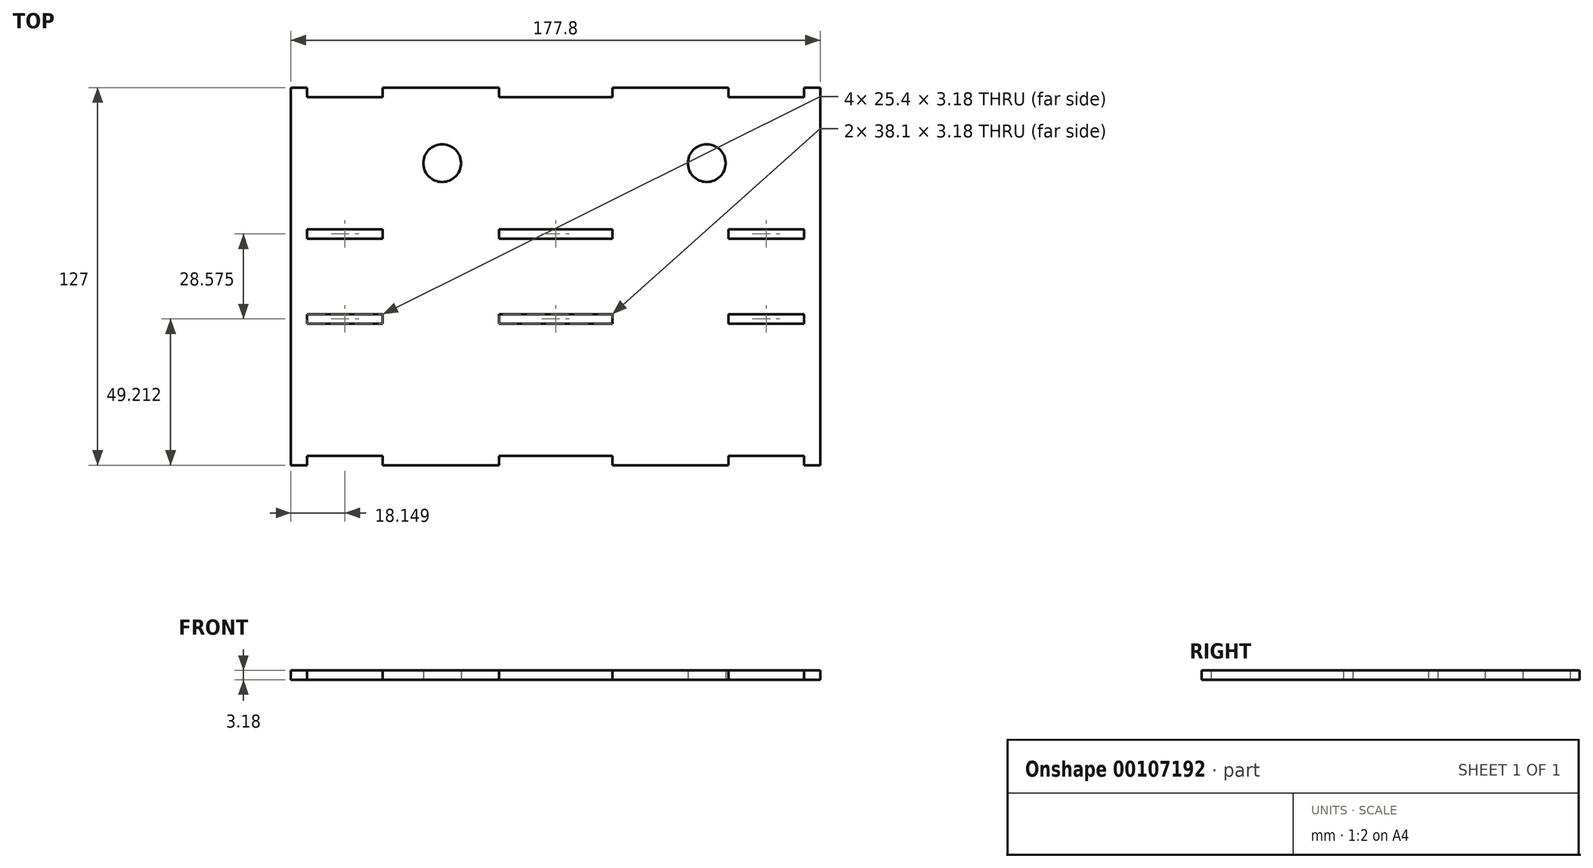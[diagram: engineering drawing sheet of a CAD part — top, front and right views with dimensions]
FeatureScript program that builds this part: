
annotation { "Feature Type Name" : "Feature", "Feature Type Description" : "" }
export const myFeature = defineFeature(function(context is Context, id is Id, definition is map)
    precondition{}
    {
        {
            var Q0;
            Q0=qCreatedBy(makeId("Top.planeOp"),FACE);
            var sketch = newSketch(context, id + "F0", { "sketchPlane" : qUnion([Q0])});
            skCircle(sketch, "E0", {"center": v(63.5, 38.1) * mm, "radius": 6.35 * mm});
            skCircle(sketch, "E1", {"center": v(-25.4, 38.1) * mm, "radius": 6.35 * mm});
            skLineSegment(sketch, "E2", {"start": v(-76.2, 63.5) * mm, "end": v(-76.2, -63.5) * mm});
            skLineSegment(sketch, "E3.bottom", {"start": v(-76.2, 63.5) * mm, "end": v(-70.75, 63.5) * mm});
            skLineSegment(sketch, "E3.left", {"start": v(-76.2, 63.5) * mm, "end": v(-76.2, -88.9) * mm});
            skLineSegment(sketch, "E3.right", {"start": v(101.6, 63.5) * mm, "end": v(101.6, -63.5) * mm});
            skCircle(sketch, "E4.MirrorC", {"center": v(63.5, -38.1) * mm, "radius": 6.35 * mm});
            skCircle(sketch, "E5.MirrorC", {"center": v(-25.4, -38.1) * mm, "radius": 6.35 * mm});
            skPoint(sketch, "E6", {"position": v(12.7, 76.2) * mm});
            skPoint(sketch, "E7", {"position": v(12.7, 63.5) * mm});
            skLineSegment(sketch, "E8.MirrorCS", {"start": v(70.75, 63.5) * mm, "end": v(70.75, 60.32) * mm});
            skLineSegment(sketch, "E9.MirrorCS", {"start": v(31.75, 60.32) * mm, "end": v(-6.35, 60.32) * mm});
            skLineSegment(sketch, "E10.MirrorCS", {"start": v(-70.75, 60.32) * mm, "end": v(-45.35, 60.32) * mm});
            skLineSegment(sketch, "E11.MirrorCS", {"start": v(-6.35, 63.5) * mm, "end": v(-6.35, 60.32) * mm});
            skLineSegment(sketch, "E12.MirrorCS", {"start": v(-70.75, 63.5) * mm, "end": v(-70.75, 60.32) * mm});
            skLineSegment(sketch, "E13.MirrorCS", {"start": v(96.15, 63.5) * mm, "end": v(96.15, 60.32) * mm});
            skLineSegment(sketch, "E14.MirrorCS", {"start": v(96.15, 60.32) * mm, "end": v(70.75, 60.32) * mm});
            skLineSegment(sketch, "E15.MirrorCS", {"start": v(31.75, 63.5) * mm, "end": v(31.75, 60.32) * mm});
            skLineSegment(sketch, "E16.MirrorCS", {"start": v(-45.35, 63.5) * mm, "end": v(-45.35, 60.32) * mm});
            skLineSegment(sketch, "E17.trimOffspring", {"start": v(-45.35, 63.5) * mm, "end": v(-6.35, 63.5) * mm});
            skLineSegment(sketch, "E18.trimOffspring", {"start": v(31.75, 63.5) * mm, "end": v(70.75, 63.5) * mm});
            skLineSegment(sketch, "E19.trimOffspring", {"start": v(96.15, 63.5) * mm, "end": v(101.6, 63.5) * mm});
            skLineSegment(sketch, "E20.MirrorCS", {"start": v(96.15, 12.7) * mm, "end": v(96.15, 15.88) * mm});
            skLineSegment(sketch, "E21.MirrorCS", {"start": v(70.75, 12.7) * mm, "end": v(70.75, 15.88) * mm});
            skLineSegment(sketch, "E22.MirrorCS", {"start": v(-6.35, 12.7) * mm, "end": v(-6.35, 15.87) * mm});
            skLineSegment(sketch, "E23.MirrorCS", {"start": v(-70.75, 12.7) * mm, "end": v(-70.75, 15.88) * mm});
            skLineSegment(sketch, "E24.MirrorCS", {"start": v(-45.35, 12.7) * mm, "end": v(-45.35, 15.88) * mm});
            skLineSegment(sketch, "E25.MirrorCS", {"start": v(31.75, 12.7) * mm, "end": v(31.75, 15.87) * mm});
            skLineSegment(sketch, "E26.MirrorCS", {"start": v(-70.75, 15.88) * mm, "end": v(-45.35, 15.88) * mm});
            skLineSegment(sketch, "E27.MirrorCS", {"start": v(31.75, 15.87) * mm, "end": v(-6.35, 15.87) * mm});
            skLineSegment(sketch, "E28.MirrorCS", {"start": v(96.15, 12.7) * mm, "end": v(70.75, 12.7) * mm});
            skLineSegment(sketch, "E29.MirrorCS", {"start": v(-45.35, 12.7) * mm, "end": v(-70.75, 12.7) * mm});
            skLineSegment(sketch, "E30.MirrorCS", {"start": v(96.15, 15.88) * mm, "end": v(70.75, 15.88) * mm});
            skLineSegment(sketch, "E31.MirrorCS", {"start": v(31.75, 12.7) * mm, "end": v(-6.35, 12.7) * mm});
            skPoint(sketch, "E32.MirrorP", {"position": v(12.7, 6.76) * mm});
            skLineSegment(sketch, "E33.MirrorCS", {"start": v(-70.75, -63.5) * mm, "end": v(-70.75, -60.32) * mm});
            skLineSegment(sketch, "E34.MirrorCS", {"start": v(-76.2, -63.5) * mm, "end": v(-70.75, -63.5) * mm});
            skLineSegment(sketch, "E35.MirrorCS", {"start": v(-6.35, -63.5) * mm, "end": v(-6.35, -60.32) * mm});
            skLineSegment(sketch, "E36.MirrorCS", {"start": v(96.15, -63.5) * mm, "end": v(96.15, -60.32) * mm});
            skLineSegment(sketch, "E37.MirrorCS", {"start": v(31.75, -63.5) * mm, "end": v(31.75, -60.32) * mm});
            skLineSegment(sketch, "E38.MirrorCS", {"start": v(70.75, -63.5) * mm, "end": v(70.75, -60.32) * mm});
            skLineSegment(sketch, "E39.MirrorCS", {"start": v(96.15, -63.5) * mm, "end": v(101.6, -63.5) * mm});
            skLineSegment(sketch, "E40.MirrorCS", {"start": v(-45.35, -63.5) * mm, "end": v(-45.35, -60.32) * mm});
            skPoint(sketch, "E41.MirrorP", {"position": v(12.7, -76.2) * mm});
            skLineSegment(sketch, "E42.MirrorCS", {"start": v(31.75, -63.5) * mm, "end": v(70.75, -63.5) * mm});
            skPoint(sketch, "E43.MirrorP", {"position": v(12.7, -63.5) * mm});
            skLineSegment(sketch, "E44.MirrorCS", {"start": v(-45.35, -63.5) * mm, "end": v(-6.35, -63.5) * mm});
            skLineSegment(sketch, "E45.MirrorCS", {"start": v(-70.75, -60.32) * mm, "end": v(-45.35, -60.32) * mm});
            skLineSegment(sketch, "E46.MirrorCS", {"start": v(96.15, -60.32) * mm, "end": v(70.75, -60.32) * mm});
            skLineSegment(sketch, "E47.MirrorCS", {"start": v(31.75, -60.32) * mm, "end": v(-6.35, -60.32) * mm});
            skLineSegment(sketch, "E48.MirrorCS", {"start": v(-45.35, -12.7) * mm, "end": v(-45.35, -15.88) * mm});
            skLineSegment(sketch, "E49.MirrorCS", {"start": v(70.75, -12.7) * mm, "end": v(70.75, -15.88) * mm});
            skLineSegment(sketch, "E50.MirrorCS", {"start": v(31.75, -12.7) * mm, "end": v(31.75, -15.87) * mm});
            skLineSegment(sketch, "E51.MirrorCS", {"start": v(-70.75, -12.7) * mm, "end": v(-70.75, -15.88) * mm});
            skLineSegment(sketch, "E52.MirrorCS", {"start": v(96.15, -12.7) * mm, "end": v(96.15, -15.88) * mm});
            skLineSegment(sketch, "E53.MirrorCS", {"start": v(-6.35, -12.7) * mm, "end": v(-6.35, -15.87) * mm});
            skLineSegment(sketch, "E54.MirrorCS", {"start": v(-70.75, -15.88) * mm, "end": v(-45.35, -15.88) * mm});
            skPoint(sketch, "E55.MirrorP", {"position": v(12.7, -6.76) * mm});
            skLineSegment(sketch, "E56.MirrorCS", {"start": v(31.75, -12.7) * mm, "end": v(-6.35, -12.7) * mm});
            skLineSegment(sketch, "E57.MirrorCS", {"start": v(31.75, -15.87) * mm, "end": v(-6.35, -15.87) * mm});
            skLineSegment(sketch, "E58.MirrorCS", {"start": v(96.15, -12.7) * mm, "end": v(70.75, -12.7) * mm});
            skLineSegment(sketch, "E59.MirrorCS", {"start": v(-45.35, -12.7) * mm, "end": v(-70.75, -12.7) * mm});
            skLineSegment(sketch, "E60.MirrorCS", {"start": v(96.15, -15.88) * mm, "end": v(70.75, -15.88) * mm});
            skSolve(sketch);
        }
        {
            var Q0;
            Q0=makeQuery(id+"F0.imprint","IMPRINT",FACE,{"disambiguationData":[TD([[makeQuery(id+"F0.imprint","IMPRINT",EDGE,{"derivedFrom":sQuery(id+"F0.wireOp",EDGE,"921fbad8-19a0-49b5-be16-62b8bbc91783")}),-1.0]])]});
            var Q1;
            Q1=makeQuery(id+"F0.imprint","IMPRINT",FACE,{"disambiguationData":[TD([[makeQuery(id+"F0.imprint","IMPRINT",EDGE,{"derivedFrom":sQuery(id+"F0.wireOp",EDGE,"E0")}),-1.0]])]});
            var Q2;
            Q2=makeQuery(id+"F0.imprint","IMPRINT",FACE,{"disambiguationData":[TD([[makeQuery(id+"F0.imprint","IMPRINT",EDGE,{"derivedFrom":sQuery(id+"F0.wireOp",EDGE,"E1")}),-1.0]])]});
            var Q3;
            Q3=makeQuery(id+"F0.imprint","IMPRINT",FACE,{"disambiguationData":[TD([[makeQuery(id+"F0.imprint","IMPRINT",EDGE,{"derivedFrom":sQuery(id+"F0.wireOp",EDGE,"E5.MirrorC")}),1.0]])]});
            var Q4;
            Q4=makeQuery(id+"F0.imprint","IMPRINT",FACE,{"disambiguationData":[TD([[makeQuery(id+"F0.imprint","IMPRINT",EDGE,{"derivedFrom":sQuery(id+"F0.wireOp",EDGE,"E4.MirrorC")}),1.0]])]});
            extrude(context, id + "F1", {"entities" : qUnion([Q0, Q1, Q2, Q3, Q4]), "depth" : 3.17 * mm});
        }
    });
